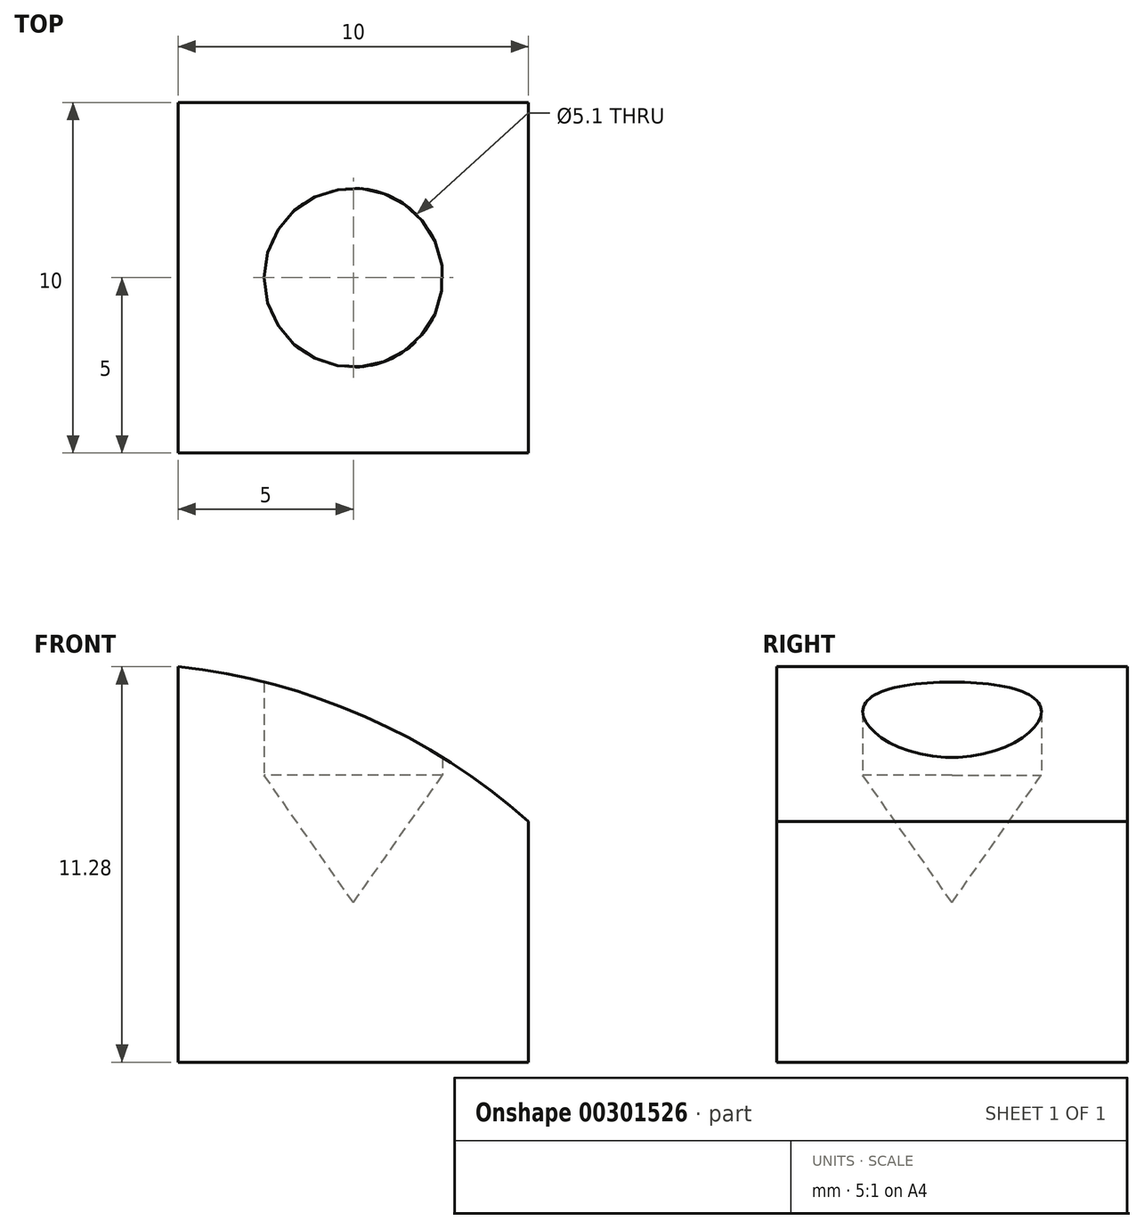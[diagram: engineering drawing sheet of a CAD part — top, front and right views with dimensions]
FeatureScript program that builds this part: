
annotation { "Feature Type Name" : "Feature", "Feature Type Description" : "" }
export const myFeature = defineFeature(function(context is Context, id is Id, definition is map)
    precondition{}
    {
        {
            var Q0;
            Q0=qCreatedBy(makeId("Top.planeOp"),FACE);
            var sketch = newSketch(context, id + "F0", { "sketchPlane" : qUnion([Q0])});
            skLineSegment(sketch, "E0.bottom", {"start": v(5, -5) * mm, "end": v(-5, -5) * mm});
            skLineSegment(sketch, "E0.top", {"start": v(5, 5) * mm, "end": v(-5, 5) * mm});
            skLineSegment(sketch, "E0.left", {"start": v(5, -5) * mm, "end": v(5, 5) * mm});
            skLineSegment(sketch, "E0.right", {"start": v(-5, -5) * mm, "end": v(-5, 5) * mm});
            skPoint(sketch, "E1", {"position": v(5, 0) * mm});
            skPoint(sketch, "E2", {"position": v(0, 5) * mm});
            skSolve(sketch);
        }
        {
            var Q0;
            Q0 = qSketchRegion(id + "F0", true);
            extrude(context, id + "F1", {"entities" : qUnion([Q0]), "depth" : 25 * mm, "hasSecondDirection" : true, "secondDirectionOppositeDirection" : true, "secondDirectionDepth" : 5 * mm});
        }
        {
            var Q0;
            Q0=qCreatedBy(makeId("Front.planeOp"),FACE);
            var sketch = newSketch(context, id + "F2", { "sketchPlane" : qUnion([Q0])});
            skLineSegment(sketch, "E3", {"start": v(0, 0) * mm, "end": v(5, 0) * mm});
            skLineSegment(sketch, "E4", {"start": v(2.55, 25) * mm, "end": v(2.55, 8.64) * mm});
            skLineSegment(sketch, "E5", {"start": v(2.55, 8.64) * mm, "end": v(0, 5) * mm});
            skLineSegment(sketch, "E6", {"start": v(0, 5) * mm, "end": v(0, 0) * mm});
            skLineSegment(sketch, "E7", {"start": v(2.55, 25) * mm, "end": v(0, 25) * mm});
            skLineSegment(sketch, "E8", {"start": v(0, 25) * mm, "end": v(0, 5) * mm});
            skSolve(sketch);
        }
        {
            var Q0;
            Q0 = qSketchRegion(id + "F2", true);
            var Q1;
            Q1=sQuery(id+"F2.wireOp",EDGE,"E8");
            revolve(context, id + "F3", {"operationType" : NewBodyOperationType.REMOVE, "entities" : qUnion([Q0]), "axis" : qUnion([Q1]), "revolveType" : RevolveType.FULL, "oppositeDirection" : true});
        }
        {
            var Q0;
            Q0=qCreatedBy(makeId("Front.planeOp"),FACE);
            var sketch = newSketch(context, id + "F4", { "sketchPlane" : qUnion([Q0])});
            skArc(sketch, "E9", {"start": v(5, 7.32) * mm, "mid": v(0.34, 10.3) * mm, "end": v(-5, 11.73) * mm});
            skPoint(sketch, "E10", {"position": v(2.55, 9.14) * mm});
            skPoint(sketch, "E11", {"position": v(-2.45, 11.27) * mm});
            skPoint(sketch, "E12", {"position": v(2.55, 8.64) * mm});
            skLineSegment(sketch, "E13", {"start": v(-5, 11.73) * mm, "end": v(-5, 25) * mm});
            skLineSegment(sketch, "E14", {"start": v(-5, 25) * mm, "end": v(5, 25) * mm});
            skLineSegment(sketch, "E15", {"start": v(5, 25) * mm, "end": v(5, 7.32) * mm});
            skLineSegment(sketch, "E16", {"start": v(5, 0.45) * mm, "end": v(-5, 0.45) * mm});
            skLineSegment(sketch, "E17", {"start": v(-5, 0.45) * mm, "end": v(-5, -5) * mm});
            skLineSegment(sketch, "E18", {"start": v(-5, -5) * mm, "end": v(5, -5) * mm});
            skLineSegment(sketch, "E19", {"start": v(5, -5) * mm, "end": v(5, 0.45) * mm});
            skSolve(sketch);
        }
        {
            var Q0;
            Q0 = qSketchRegion(id + "F4", true);
            extrude(context, id + "F5", {"entities" : qUnion([Q0]), "operationType" : NewBodyOperationType.REMOVE, "oppositeDirection" : true, "depth" : 25 * mm, "hasSecondDirection" : true, "secondDirectionOppositeDirection" : false, "secondDirectionDepth" : 25 * mm});
        }
    });
